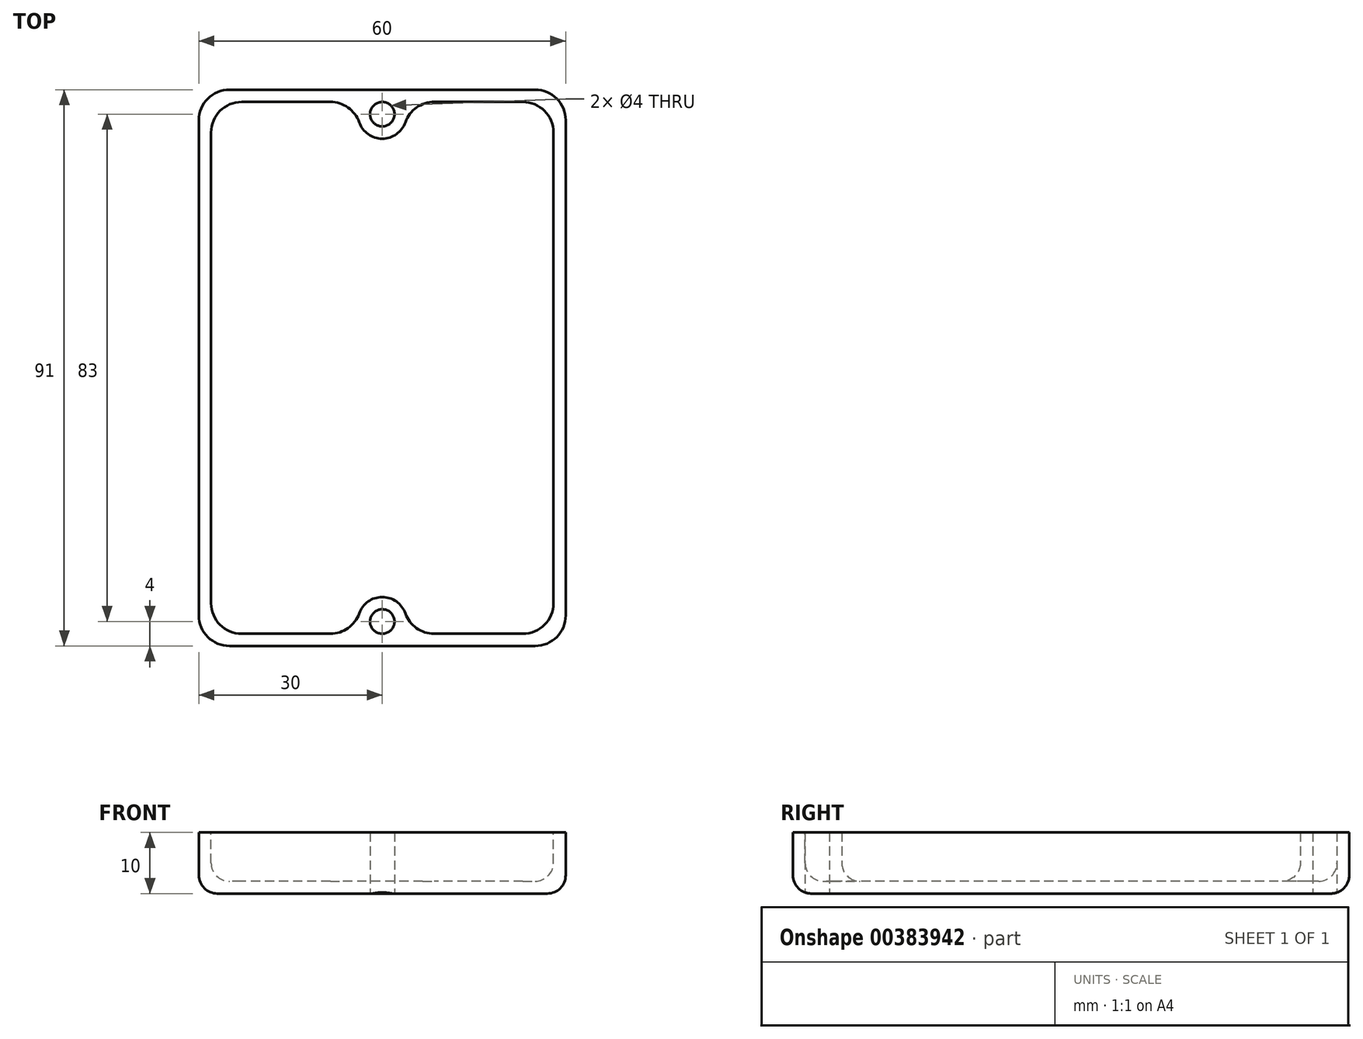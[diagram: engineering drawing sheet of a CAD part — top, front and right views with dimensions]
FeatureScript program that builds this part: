
annotation { "Feature Type Name" : "Feature", "Feature Type Description" : "" }
export const myFeature = defineFeature(function(context is Context, id is Id, definition is map)
    precondition{}
    {
        {
            assignVariable(context, id + "F0", {"name" : "lidwallthickness", "anyValue" : 2});
        }
        {
            assignVariable(context, id + "F1", {"name" : "lidheight", "anyValue" : 10});
        }
        {
            assignVariable(context, id + "F2", {"name" : "filletradius", "anyValue" : 3});
        }
        {
            var Q0;
            Q0=qCreatedBy(makeId("Top.planeOp"),FACE);
            var sketch = newSketch(context, id + "F3", { "sketchPlane" : qUnion([Q0])});
            skLineSegment(sketch, "E0.bottom", {"start": v(30, 45.5) * mm, "end": v(-30, 45.5) * mm});
            skLineSegment(sketch, "E0.top", {"start": v(30, -45.5) * mm, "end": v(-30, -45.5) * mm});
            skLineSegment(sketch, "E0.left", {"start": v(30, 45.5) * mm, "end": v(30, -45.5) * mm});
            skLineSegment(sketch, "E0.right", {"start": v(-30, 45.5) * mm, "end": v(-30, -45.5) * mm});
            skPoint(sketch, "E0.middle", {"position": v(0, 0) * mm});
            skSolve(sketch);
        }
        {
            var Q0;
            Q0=qSketchRegion(id+"F3",true);
            extrude(context, id + "F4", {"entities" : qUnion([Q0]), "depth" : (getVariable(context, 'lidheight')) * mm});
        }
        {
            var Q0;
            Q0=makeQuery(id+"F4.opExtrude","CAP_FACE",FACE,{"disambiguationData":[OSD([sQuery(id+"F3.wireOp",EDGE,"E0.bottom"),sQuery(id+"F3.wireOp",EDGE,"E0.top"),sQuery(id+"F3.wireOp",EDGE,"E0.left"),sQuery(id+"F3.wireOp",EDGE,"E0.right")])],"isStart":false});
            var sketch = newSketch(context, id + "F5", { "sketchPlane" : qUnion([Q0])});
            skLineSegment(sketch, "E1.bottom", {"start": v(28, 43.5) * mm, "end": v(-28, 43.5) * mm});
            skLineSegment(sketch, "E1.top", {"start": v(28, -43.5) * mm, "end": v(-28, -43.5) * mm});
            skLineSegment(sketch, "E1.left", {"start": v(28, 43.5) * mm, "end": v(28, -43.5) * mm});
            skLineSegment(sketch, "E1.right", {"start": v(-28, 43.5) * mm, "end": v(-28, -43.5) * mm});
            skPoint(sketch, "E1.middle", {"position": v(0, 0) * mm});
            skSolve(sketch);
        }
        {
            var Q0;
            Q0=qSketchRegion(id+"F5",true);
            extrude(context, id + "F6", {"entities" : qUnion([Q0]), "operationType" : NewBodyOperationType.REMOVE, "oppositeDirection" : true, "depth" : (getVariable(context, 'lidheight') - getVariable(context, 'lidwallthickness')) * mm});
        }
        {
            var Q0;
            Q0=makeQuery(id+"F4.opExtrude","CAP_FACE",FACE,{"disambiguationData":[OSD([sQuery(id+"F3.wireOp",EDGE,"E0.bottom"),sQuery(id+"F3.wireOp",EDGE,"E0.top"),sQuery(id+"F3.wireOp",EDGE,"E0.left"),sQuery(id+"F3.wireOp",EDGE,"E0.right")])],"isStart":true});
            var sketch = newSketch(context, id + "F7", { "sketchPlane" : qUnion([Q0])});
            skCircle(sketch, "E2", {"center": v(0, -41.5) * mm, "radius": 4 * mm});
            skCircle(sketch, "E3.MirrorC", {"center": v(0, 41.5) * mm, "radius": 4 * mm});
            skSolve(sketch);
        }
        {
            var Q0;
            Q0=qSketchRegion(id+"F7",true);
            extrude(context, id + "F8", {"entities" : qUnion([Q0]), "operationType" : NewBodyOperationType.ADD, "oppositeDirection" : true, "depth" : (getVariable(context, 'lidheight')) * mm});
        }
        {
            var Q0;
            Q0=makeQuery(id+"F4.opExtrude","CAP_FACE",FACE,{"disambiguationData":[OSD([sQuery(id+"F3.wireOp",EDGE,"E0.bottom"),sQuery(id+"F3.wireOp",EDGE,"E0.top"),sQuery(id+"F3.wireOp",EDGE,"E0.left"),sQuery(id+"F3.wireOp",EDGE,"E0.right")])],"isStart":true});
            var sketch = newSketch(context, id + "F9", { "sketchPlane" : qUnion([Q0])});
            skCircle(sketch, "E4", {"center": v(0, -41.5) * mm, "radius": 2 * mm});
            skPoint(sketch, "E4.centerSnap0", {"position": v(0, -45.5) * mm});
            skCircle(sketch, "E5.MirrorC", {"center": v(0, 41.5) * mm, "radius": 2 * mm});
            skSolve(sketch);
        }
        {
            var Q0;
            Q0=qSketchRegion(id+"F9",true);
            extrude(context, id + "F10", {"entities" : qUnion([Q0]), "operationType" : NewBodyOperationType.REMOVE, "endBound" : BoundingType.THROUGH_ALL, "oppositeDirection" : true, "depth" : 25 * mm});
        }
        {
            var Q0;
            Q0=makeQuery(id+"F8.boolean.opBoolean","INTERSECT",EDGE,{"disambiguationData":[OD(1.0)],"derivedFrom":[makeQuery(id+"F6.boolean.opBoolean","COPY",FACE,{"derivedFrom":makeQuery(id+"F6.opExtrude","SWEPT_FACE",FACE,{"disambiguationData":[OSD([sQuery(id+"F5.wireOp",EDGE,"E1.bottom")])]})}),makeQuery(id+"F8.opExtrude","SWEPT_FACE",FACE,{"disambiguationData":[OSD([sQuery(id+"F7.wireOp",EDGE,"E2")])]})]});
            var Q1;
            Q1=makeQuery(id+"F8.boolean.opBoolean","INTERSECT",EDGE,{"disambiguationData":[OD(0.0)],"derivedFrom":[makeQuery(id+"F6.boolean.opBoolean","COPY",FACE,{"derivedFrom":makeQuery(id+"F6.opExtrude","SWEPT_FACE",FACE,{"disambiguationData":[OSD([sQuery(id+"F5.wireOp",EDGE,"E1.bottom")])]})}),makeQuery(id+"F8.opExtrude","SWEPT_FACE",FACE,{"disambiguationData":[OSD([sQuery(id+"F7.wireOp",EDGE,"E2")])]})]});
            var Q2;
            Q2=makeQuery(id+"F8.boolean.opBoolean","INTERSECT",EDGE,{"disambiguationData":[OD(0.0)],"derivedFrom":[makeQuery(id+"F6.boolean.opBoolean","COPY",FACE,{"derivedFrom":makeQuery(id+"F6.opExtrude","SWEPT_FACE",FACE,{"disambiguationData":[OSD([sQuery(id+"F5.wireOp",EDGE,"E1.top")])]})}),makeQuery(id+"F8.opExtrude","SWEPT_FACE",FACE,{"disambiguationData":[OSD([sQuery(id+"F7.wireOp",EDGE,"E3.MirrorC")])]})]});
            var Q3;
            Q3=makeQuery(id+"F8.boolean.opBoolean","INTERSECT",EDGE,{"disambiguationData":[OD(1.0)],"derivedFrom":[makeQuery(id+"F6.boolean.opBoolean","COPY",FACE,{"derivedFrom":makeQuery(id+"F6.opExtrude","SWEPT_FACE",FACE,{"disambiguationData":[OSD([sQuery(id+"F5.wireOp",EDGE,"E1.top")])]})}),makeQuery(id+"F8.opExtrude","SWEPT_FACE",FACE,{"disambiguationData":[OSD([sQuery(id+"F7.wireOp",EDGE,"E3.MirrorC")])]})]});
            fillet(context, id + "F11", {"entities" : qUnion([Q0, Q1, Q2, Q3]), "radius" : 5 * mm, "tangentPropagation" : true, "allowEdgeOverflow" : false});
        }
        {
            var Q0;
            Q0=makeQuery(id+"F4.opExtrude","SWEPT_EDGE",EDGE,{"disambiguationData":[OSD([sQuery(id+"F3.wireOp",EDGE,"E0.top"),sQuery(id+"F3.wireOp",EDGE,"E0.left")])]});
            var Q1;
            Q1=makeQuery(id+"F4.opExtrude","SWEPT_EDGE",EDGE,{"disambiguationData":[OSD([sQuery(id+"F3.wireOp",EDGE,"E0.top"),sQuery(id+"F3.wireOp",EDGE,"E0.right")])]});
            var Q2;
            Q2=makeQuery(id+"F4.opExtrude","SWEPT_EDGE",EDGE,{"disambiguationData":[OSD([sQuery(id+"F3.wireOp",EDGE,"E0.bottom"),sQuery(id+"F3.wireOp",EDGE,"E0.left")])]});
            var Q3;
            Q3=makeQuery(id+"F4.opExtrude","SWEPT_EDGE",EDGE,{"disambiguationData":[OSD([sQuery(id+"F3.wireOp",EDGE,"E0.bottom"),sQuery(id+"F3.wireOp",EDGE,"E0.right")])]});
            var Q4;
            Q4=makeQuery(id+"F6.boolean.opBoolean","COPY",EDGE,{"derivedFrom":makeQuery(id+"F6.opExtrude","SWEPT_EDGE",EDGE,{"disambiguationData":[OSD([sQuery(id+"F5.wireOp",EDGE,"E1.top"),sQuery(id+"F5.wireOp",EDGE,"E1.left")])]})});
            var Q5;
            Q5=makeQuery(id+"F6.boolean.opBoolean","COPY",EDGE,{"derivedFrom":makeQuery(id+"F6.opExtrude","SWEPT_EDGE",EDGE,{"disambiguationData":[OSD([sQuery(id+"F5.wireOp",EDGE,"E1.top"),sQuery(id+"F5.wireOp",EDGE,"E1.right")])]})});
            var Q6;
            Q6=makeQuery(id+"F6.boolean.opBoolean","COPY",EDGE,{"derivedFrom":makeQuery(id+"F6.opExtrude","SWEPT_EDGE",EDGE,{"disambiguationData":[OSD([sQuery(id+"F5.wireOp",EDGE,"E1.bottom"),sQuery(id+"F5.wireOp",EDGE,"E1.right")])]})});
            var Q7;
            Q7=makeQuery(id+"F6.boolean.opBoolean","COPY",EDGE,{"derivedFrom":makeQuery(id+"F6.opExtrude","SWEPT_EDGE",EDGE,{"disambiguationData":[OSD([sQuery(id+"F5.wireOp",EDGE,"E1.bottom"),sQuery(id+"F5.wireOp",EDGE,"E1.left")])]})});
            fillet(context, id + "F12", {"entities" : qUnion([Q0, Q1, Q2, Q3, Q4, Q5, Q6, Q7]), "radius" : 5 * mm, "tangentPropagation" : true, "allowEdgeOverflow" : false});
        }
        {
            var Q0;
            Q0=makeQuery(id+"F6.boolean.opBoolean","COPY",EDGE,{"derivedFrom":makeQuery(id+"F6.opExtrude","CAP_EDGE",EDGE,{"disambiguationData":[OSD([sQuery(id+"F5.wireOp",EDGE,"E1.right")])],"isStart":false})});
            var Q1;
            Q1=makeQuery(id+"F4.opExtrude","CAP_EDGE",EDGE,{"disambiguationData":[OSD([sQuery(id+"F3.wireOp",EDGE,"E0.left")])],"isStart":true});
            fillet(context, id + "F13", {"entities" : qUnion([Q0, Q1]), "radius" : (getVariable(context, 'filletradius')) * mm, "tangentPropagation" : true, "allowEdgeOverflow" : false});
        }
    });
